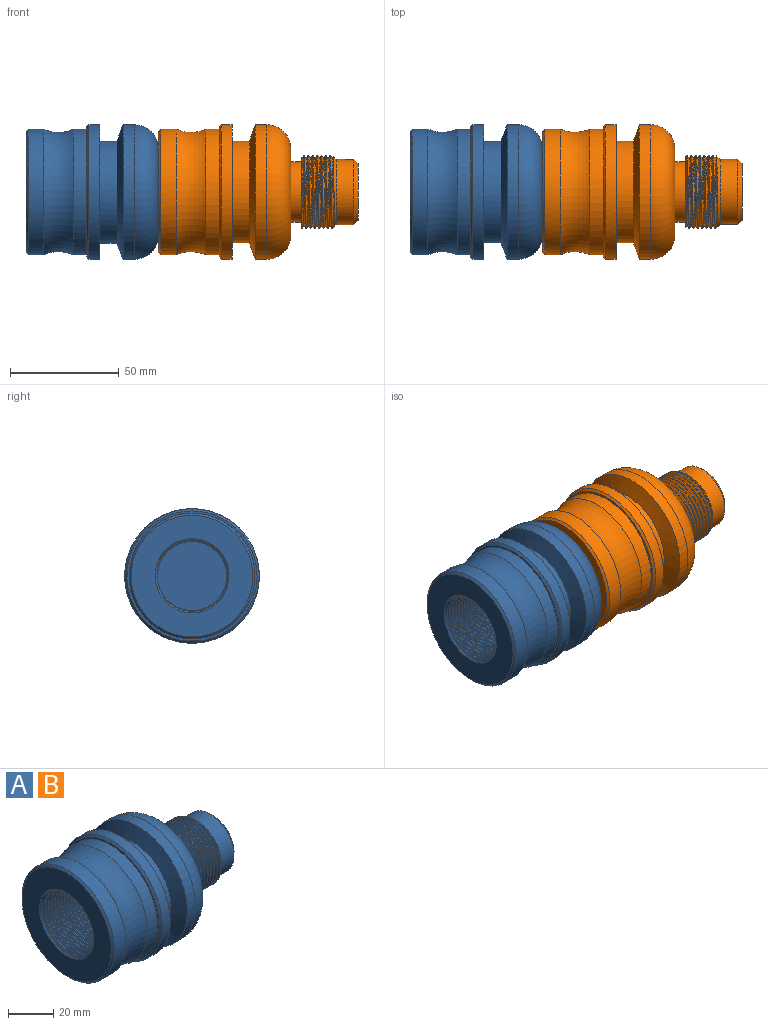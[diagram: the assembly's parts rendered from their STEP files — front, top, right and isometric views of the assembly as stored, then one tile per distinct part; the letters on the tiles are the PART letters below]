
ASSEMBLY  parts=2 mates=1
PART A: 45 faces, bbox 93.4x70.2x70.2 mm
  f0: cylinder r=17mm len=34mm, axis (1,0,0), area 104.7mm2, adj f3,f4,f19,f41
  f1: plane 56.01x56.01mm, normal (-1,0,0), area 1553.2mm2, adj f5,f6,f32,f34,f40
  f2: bspline ~36.76x31.84mm, area 417.2mm2, adj f3,f4,f19,f41
  f3: bspline ~39.26x34mm, area 938.2mm2, adj f0,f2,f19,f41
  f4: bspline ~39.26x34mm, area 945.7mm2, adj f0,f2,f19,f41
  f5: bspline ~39.45x34.17mm, area 1509.3mm2, adj f1,f7,f8,f9,f10,f11,f12,f13
  f6: bspline ~39.45x34.17mm, area 1451.8mm2, adj f1,f8,f9,f10,f11,f12,f13,f14
  f7: cylinder r=16mm len=32mm, axis (-1,0,0), area 1400.9mm2, adj f5,f8,f35,f36,f38,f39
  f8: cylinder r=16mm len=32mm, axis (-1,0,0), area 52.1mm2, adj f5,f6,f7,f9,f35
  f9: cylinder r=16mm len=32mm, axis (-1,0,0), area 50.2mm2, adj f5,f6,f8,f10
  f10: cylinder r=16mm len=32mm, axis (-1,0,0), area 50.3mm2, adj f5,f6,f9,f11
  f11: cylinder r=16mm len=32mm, axis (-1,0,0), area 50.3mm2, adj f5,f6,f10,f12
  f12: cylinder r=16mm len=32mm, axis (-1,0,0), area 50.3mm2, adj f5,f6,f11,f13
  f13: cylinder r=16mm len=32mm, axis (-1,0,0), area 50.3mm2, adj f5,f6,f12,f14
  f14: cylinder r=16mm len=32mm, axis (-1,0,0), area 50.3mm2, adj f5,f6,f13,f15
  f15: cylinder r=16mm len=32mm, axis (-1,0,0), area 50.3mm2, adj f5,f6,f14,f16
  f16: cylinder r=16mm len=32mm, axis (-1,0,0), area 50.3mm2, adj f5,f6,f15,f17
  f17: cylinder r=16mm len=32mm, axis (-1,0,0), area 50.3mm2, adj f5,f6,f16,f18
  f18: cylinder r=16mm len=32mm, axis (-1,0,0), area 44mm2, adj f5,f6,f17,f40
  f19: plane 33.44x33.33mm, normal (-1,0,0), area 227mm2, adj f0,f2,f3,f4,f20
  f20: cylinder r=14mm len=28mm, axis (1,0,0), area 439.8mm2, adj f19,f21
  f21: plane 40x40mm, normal (1,0,0), area 640.9mm2, adj f20,f31
  f22: cylinder r=31mm len=62mm, axis (1,0,0), area 1026.5mm2, adj f23,f31
  f23: cone r=31mm half-angle=70deg, axis (1,0,0), area 1366.5mm2, adj f22,f24
  f24: cylinder r=23.5mm len=47mm, axis (1,0,0), area 1181.2mm2, adj f23,f25
  f25: plane 62x62mm, normal (1,0,0), area 1284.1mm2, adj f24,f26
  f26: cylinder r=31mm len=62mm, axis (1,0,0), area 973.9mm2, adj f25,f33
  f27: plane 60x60mm, normal (-1,0,0), area 185.4mm2, adj f28,f33
  f28: cylinder r=29mm len=58mm, axis (1,0,0), area 1136.3mm2, adj f27,f29
  f29: torus R=43.5mm, axis (1,0,0), area 2457.5mm2, adj f28,f30
  f30: cylinder r=29mm len=58mm, axis (1,0,0), area 1318.5mm2, adj f29,f32
  f31: torus R=20mm, axis (1,0,0), area 2931.6mm2, adj f21,f22
  f32: cone r=29mm half-angle=45deg, axis (1,0,0), area 253.2mm2, adj f1,f30
  f33: cone r=31mm half-angle=45deg, axis (1,0,0), area 271mm2, adj f26,f27
  f34: bspline ~39.66x34.35mm, area 362mm2, adj f1,f5,f6,f37
  f35: bspline ~33.8x33.44mm, area 69.1mm2, adj f6,f7,f8,f37,f38
  f36: bspline ~33.8x33.44mm, area 69.1mm2, adj f5,f7,f37,f38
  f37: bspline ~33.99x33.62mm, area 30.3mm2, adj f34,f35,f36,f38
  f38: plane 0.35x0.15mm, normal (0,-1,0), area 0mm2, adj f7,f35,f36,f37
  f39: plane 32x32mm, normal (-1,0,0), area 804.2mm2, adj f7
  f40: cone r=15mm half-angle=45deg, axis (-1,0,0), area 79.4mm2, adj f1,f5,f6,f18
  f41: cone r=17mm half-angle=45deg, axis (-1,0,0), area 194.7mm2, adj f0,f2,f3,f4,f44
  f42: plane 26x26mm, normal (1,0,0), area 530.9mm2, adj f43
  f43: cone r=13mm half-angle=45deg, axis (-1,0,0), area 248.8mm2, adj f42,f44
  f44: cylinder r=15mm len=30mm, axis (1,0,0), area 754mm2, adj f41,f43
PART B: same geometry as A
PLACE A t=(-61,-0.01,-0.01)mm
PLACE B at identity fixed
MATE fastened B.f1 <-> A.f0  axis (-1,0,0) through (-92,-0.01,-0.01)mm
